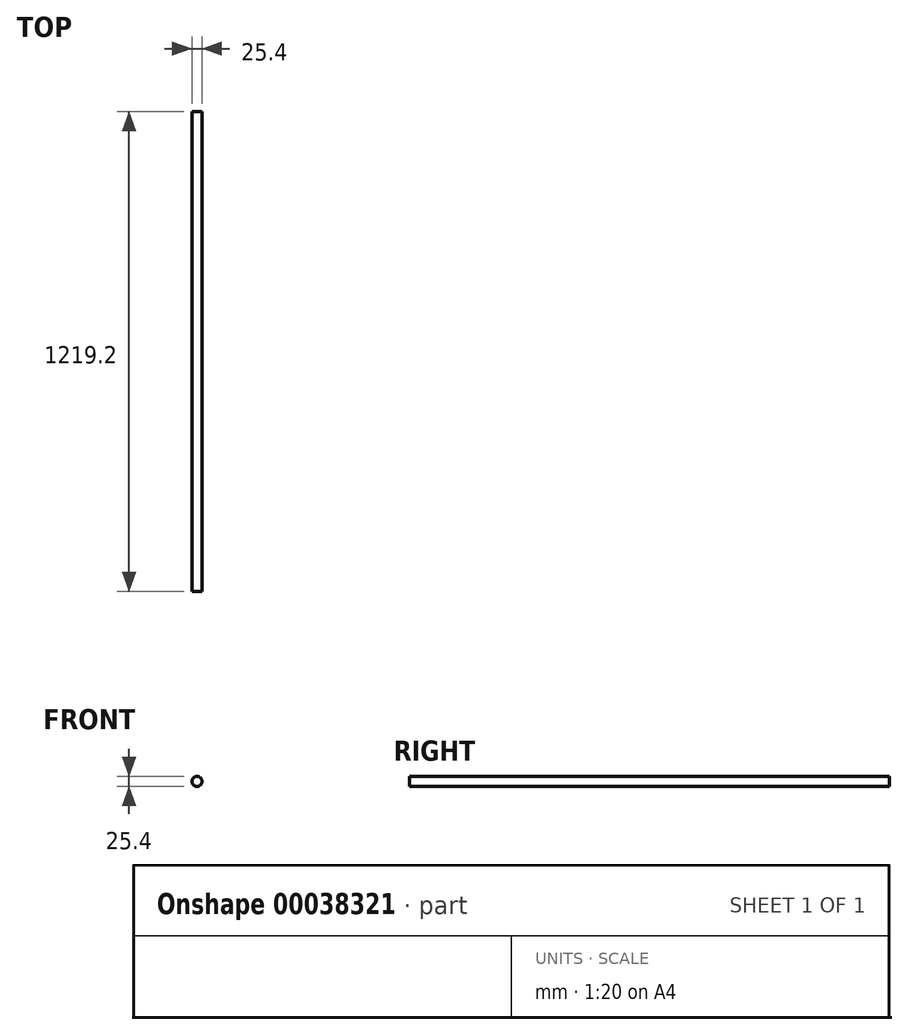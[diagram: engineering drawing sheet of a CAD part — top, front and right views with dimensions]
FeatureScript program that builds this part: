
annotation { "Feature Type Name" : "Feature", "Feature Type Description" : "" }
export const myFeature = defineFeature(function(context is Context, id is Id, definition is map)
    precondition{}
    {
        {
            var Q0;
            Q0=qCreatedBy(makeId("Front.planeOp"),FACE);
            var sketch = newSketch(context, id + "F0", { "sketchPlane" : qUnion([Q0])});
            skLineSegment(sketch, "E0", {"start": v(457.2, -652.17) * mm, "end": v(470.26, -652.17) * mm});
            skLineSegment(sketch, "E1", {"start": v(444.5, -652.17) * mm, "end": v(457.2, -652.17) * mm});
            skCircle(sketch, "E2", {"center": v(-708.45, 74.17) * mm, "radius": 12.7 * mm});
            skSolve(sketch);
        }
        {
            var Q0;
            Q0 = qSketchRegion(id + "F0", true);
            extrude(context, id + "F1", {"entities" : qUnion([Q0]), "depth" : 1219.2 * mm});
        }
    });
